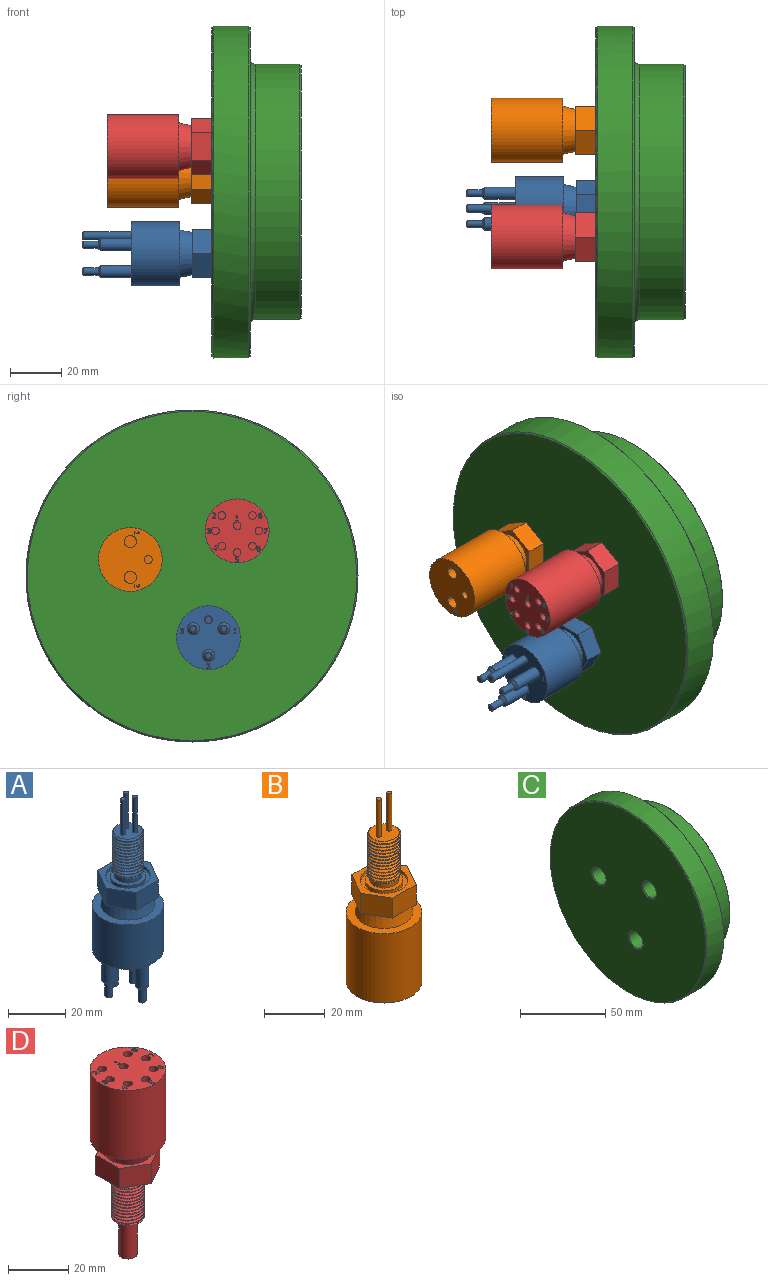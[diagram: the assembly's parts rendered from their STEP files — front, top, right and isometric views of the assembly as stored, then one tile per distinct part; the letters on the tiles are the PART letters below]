
ASSEMBLY  parts=4 mates=6
PART A: 107 faces, bbox 25.1x25.1x84.6 mm
  f0: bspline ~17.61x11.58mm, area 383.2mm2, adj f1,f2,f3,f4,f5,f6
  f1: cone r=5.31mm half-angle=45deg, axis (0,0,1), area 12.2mm2, adj f0,f2,f5,f6
  f2: cylinder r=5.56mm len=16mm, axis (0,0,1), area 187mm2, adj f0,f1,f3,f5
  f3: cone r=5.31mm half-angle=45deg, axis (0,0,-1), area 12.2mm2, adj f0,f2,f4,f5
  f4: plane 10.16x9.91mm, normal (0,0,1), area 72.4mm2, adj f0,f3,f5,f7,f8,f9
  f5: bspline ~17.61x11.58mm, area 382.1mm2, adj f0,f1,f2,f3,f4,f6
  f6: plane 10.17x10.16mm, normal (0,0,-1), area 79.2mm2, adj f0,f1,f5
  f7: cylinder r=0.85mm len=15mm, axis (0,0,1), area 80.1mm2, adj f4,f10
  f8: cylinder r=0.85mm len=15mm, axis (0,0,1), area 80.1mm2, adj f4,f11
  f9: cylinder r=0.85mm len=15mm, axis (0,0,1), area 80.1mm2, adj f4,f12
  f10: plane 1.7x1.7mm, normal (0,0,1), area 2.3mm2, adj f7
  f11: plane 1.7x1.7mm, normal (0,0,1), area 2.3mm2, adj f8
  f12: plane 1.7x1.7mm, normal (0,0,1), area 2.3mm2, adj f9
  f13: plane 9.56x9.56mm, normal (0,0,1), area 71.7mm2, adj f14
  f14: cylinder r=4.78mm len=9.56mm, axis (0,0,-1), area 60mm2, adj f13,f15
  f15: plane 12.5x12.5mm, normal (0,0,1), area 51mm2, adj f14,f16
  f16: cylinder r=6.25mm len=12.5mm, axis (0,0,-1), area 51.1mm2, adj f15,f17
  f17: plane 15.7x15.7mm, normal (0,0,1), area 70.9mm2, adj f16,f18
  f18: cylinder r=7.85mm len=15.7mm, axis (0,0,-1), area 64.1mm2, adj f17,f19
  f19: plane 21.94x19mm, normal (0,0,1), area 119mm2, adj f18,f20,f21,f22,f23,f24,f25
  f20: plane 10.97x7.5mm, normal (0,1,0), area 82.3mm2, adj f19,f21,f25,f26
  f21: plane 9.5x7.5mm, normal (-0.87,0.5,0), area 82.3mm2, adj f19,f20,f22,f26
  f22: plane 9.5x7.5mm, normal (-0.87,-0.5,0), area 82.3mm2, adj f19,f21,f23,f26
  f23: plane 10.97x7.5mm, normal (0,-1,0), area 82.3mm2, adj f19,f22,f24,f26
  f24: plane 9.5x7.5mm, normal (0.87,-0.5,0), area 82.3mm2, adj f19,f23,f25,f26
  f25: plane 9.5x7.5mm, normal (0.87,0.5,0), area 82.3mm2, adj f19,f20,f24,f26
  f26: plane 21.94x19mm, normal (0,0,-1), area 98.8mm2, adj f20,f21,f22,f23,f24,f25,f27
  f27: cone r=9.5mm half-angle=14deg, axis (0,0,-1), area 287.4mm2, adj f26,f28
  f28: plane 25x25mm, normal (0,0,1), area 207.3mm2, adj f27,f29
  f29: cylinder r=12.5mm len=25mm, axis (0,0,1), area 1492.3mm2, adj f28,f30
  f30: plane 25x25mm, normal (0,0,-1), area 425.9mm2, adj f29,f31,f32,f33,f34,f35,f36,f37
  f31: plane 0.23x0.1mm, normal (1,0,0), area 0mm2, adj f30,f32,f47,f90
  f32: plane 1.23x0.1mm, normal (0,1,0), area 0.1mm2, adj f30,f31,f33,f90
  f33: plane 0.28x0.1mm, normal (-1,0,0), area 0mm2, adj f30,f32,f34,f90
  f34: extruded ~0.48x0.48mm, area 0.1mm2, adj f30,f33,f35,f90
  f35: extruded ~0.71x0.4mm, area 0.1mm2, adj f30,f34,f36,f90
  f36: extruded ~0.25x0.1mm, area 0mm2, adj f30,f35,f37,f90
  f37: extruded ~0.24x0.1mm, area 0mm2, adj f30,f36,f38,f90
  f38: extruded ~0.28x0.1mm, area 0mm2, adj f30,f37,f39,f90
  f39: extruded ~0.19x0.11mm, area 0mm2, adj f30,f38,f40,f90
  f40: plane 0.1x0.01mm, normal (0,1,0), area 0mm2, adj f30,f39,f41,f90
  f41: plane 0.29x0.1mm, normal (-1,0,0), area 0mm2, adj f30,f40,f42,f90
  f42: extruded ~0.51x0.12mm, area 0.1mm2, adj f30,f41,f43,f90
  f43: extruded ~0.6x0.55mm, area 0.1mm2, adj f30,f42,f44,f90
  f44: extruded ~0.4x0.1mm, area 0mm2, adj f30,f43,f45,f90
  f45: extruded ~0.34x0.27mm, area 0mm2, adj f30,f44,f46,f90
  f46: extruded ~0.53x0.52mm, area 0.1mm2, adj f30,f45,f47,f90
  f47: plane 0.98x0.1mm, normal (0,-1,0), area 0.1mm2, adj f30,f31,f46,f90
  f48: plane 0.2x0.1mm, normal (1,0,0), area 0mm2, adj f30,f49,f58,f91
  f49: plane 0.98x0.1mm, normal (0,1,0), area 0.1mm2, adj f30,f48,f50,f91
  f50: plane 0.2x0.1mm, normal (-1,0,0), area 0mm2, adj f30,f49,f51,f91
  f51: plane 0.36x0.1mm, normal (0,-1,0), area 0mm2, adj f30,f50,f52,f91
  f52: plane 1.34x0.1mm, normal (-1,0,0), area 0.1mm2, adj f30,f51,f53,f91
  f53: plane 0.36x0.1mm, normal (0,1,0), area 0mm2, adj f30,f52,f54,f91
  f54: plane 0.18x0.1mm, normal (-1,0,0), area 0mm2, adj f30,f53,f55,f91
  f55: extruded ~0.41x0.28mm, area 0.1mm2, adj f30,f54,f56,f91
  f56: plane 0.21x0.1mm, normal (0,-1,0), area 0mm2, adj f30,f55,f57,f91
  f57: plane 1.8x0.1mm, normal (1,0,0), area 0.2mm2, adj f30,f56,f58,f91
  f58: plane 0.36x0.1mm, normal (0,-1,0), area 0mm2, adj f30,f48,f57,f91
  f59: extruded ~0.24x0.1mm, area 0mm2, adj f30,f60,f85,f92
  f60: extruded ~0.29x0.1mm, area 0mm2, adj f30,f59,f61,f92
  f61: extruded ~0.2x0.11mm, area 0mm2, adj f30,f60,f62,f92
  f62: plane 0.1x0.02mm, normal (0,1,0), area 0mm2, adj f30,f61,f63,f92
  f63: plane 0.28x0.1mm, normal (-1,0,0), area 0mm2, adj f30,f62,f64,f92
  f64: extruded ~0.52x0.12mm, area 0.1mm2, adj f30,f63,f65,f92
  f65: extruded ~0.42x0.11mm, area 0mm2, adj f30,f64,f66,f92
  f66: extruded ~0.37x0.18mm, area 0mm2, adj f30,f65,f67,f92
  f67: extruded ~0.45x0.37mm, area 0.1mm2, adj f30,f66,f68,f92
  f68: plane 0.1x0.02mm, normal (1,0,0), area 0mm2, adj f30,f67,f69,f92
  f69: extruded ~0.27x0.13mm, area 0mm2, adj f30,f68,f70,f92
  f70: extruded ~0.37x0.14mm, area 0mm2, adj f30,f69,f71,f92
  f71: cylinder r=0.63mm len=0.45mm, axis (0,0,1), area 0mm2, adj f30,f70,f72,f92
  f72: extruded ~0.49x0.18mm, area 0.1mm2, adj f30,f71,f73,f92
  f73: extruded ~0.55x0.12mm, area 0.1mm2, adj f30,f72,f74,f92
  f74: plane 0.28x0.1mm, normal (-1,0,0), area 0mm2, adj f30,f73,f75,f92
  f75: plane 0.1x0.02mm, normal (0,-1,0), area 0mm2, adj f30,f74,f76,f92
  f76: extruded ~0.51x0.18mm, area 0.1mm2, adj f30,f75,f77,f92
  f77: extruded ~0.3x0.11mm, area 0mm2, adj f30,f76,f78,f92
  f78: extruded ~0.31x0.11mm, area 0mm2, adj f30,f77,f79,f92
  f79: extruded ~0.29x0.12mm, area 0mm2, adj f30,f78,f80,f92
  f80: extruded ~0.3x0.1mm, area 0mm2, adj f30,f79,f81,f92
  f81: plane 0.11x0.1mm, normal (0,1,0), area 0mm2, adj f30,f80,f82,f92
  f82: plane 0.22x0.1mm, normal (-1,0,0), area 0mm2, adj f30,f81,f83,f92
  f83: plane 0.1x0.09mm, normal (0,-1,0), area 0mm2, adj f30,f82,f84,f92
  f84: extruded ~0.41x0.34mm, area 0.1mm2, adj f30,f83,f85,f92
  f85: extruded ~0.22x0.11mm, area 0mm2, adj f30,f59,f84,f92
  f86: cylinder r=2.4mm len=12mm, axis (0,0,-1), area 181mm2, adj f30,f93
  f87: cylinder r=2.4mm len=12mm, axis (0,0,-1), area 181mm2, adj f30,f94
  f88: cylinder r=2.4mm len=12mm, axis (0,0,-1), area 181mm2, adj f30,f95
  f89: cylinder r=1.6mm len=18.7mm, axis (0,0,-1), area 188mm2, adj f30,f96
  f90: plane 2.04x1.23mm, normal (0,0,-1), area 1mm2, adj f31,f32,f33,f34,f35,f36,f37,f38
  f91: plane 2.01x0.98mm, normal (0,0,-1), area 0.7mm2, adj f48,f49,f50,f51,f52,f53,f54,f55
  f92: plane 2.08x1.22mm, normal (0,0,-1), area 1mm2, adj f59,f60,f61,f62,f63,f64,f65,f66
  f93: cone r=1.9mm half-angle=45deg, axis (0,0,1), area 16.9mm2, adj f86,f97
  f94: cone r=1.9mm half-angle=45deg, axis (0,0,1), area 16.9mm2, adj f87,f98
  f95: cone r=1.9mm half-angle=45deg, axis (0,0,1), area 16.9mm2, adj f88,f99
  f96: cone r=1.45mm half-angle=45deg, axis (0,0,1), area 3.9mm2, adj f89,f100
  f97: cylinder r=1.4mm len=5.7mm, axis (0,0,-1), area 50.1mm2, adj f93,f101
  f98: cylinder r=1.4mm len=5.7mm, axis (0,0,-1), area 50.1mm2, adj f94,f102
  f99: cylinder r=1.4mm len=5.7mm, axis (0,0,-1), area 50.1mm2, adj f95,f103
  f100: plane 2.6x2.6mm, normal (0,0,-1), area 5.3mm2, adj f96
  f101: cone r=1.25mm half-angle=45deg, axis (0,0,1), area 3.3mm2, adj f97,f104
  f102: cone r=1.25mm half-angle=45deg, axis (0,0,1), area 3.3mm2, adj f98,f105
  f103: cone r=1.25mm half-angle=45deg, axis (0,0,1), area 3.3mm2, adj f99,f106
  f104: plane 2.2x2.2mm, normal (0,0,-1), area 3.8mm2, adj f101
  f105: plane 2.2x2.2mm, normal (0,0,-1), area 3.8mm2, adj f102
  f106: plane 2.2x2.2mm, normal (0,0,-1), area 3.8mm2, adj f103
PART B: 64 faces, bbox 25.1x25.1x75.1 mm
  f0: bspline ~17.61x11.58mm, area 383.3mm2, adj f1,f2,f3,f34,f35,f36,f39
  f1: bspline ~17.61x11.58mm, area 388.6mm2, adj f0,f2,f3,f34,f35,f36
  f2: plane 10.17x10.16mm, normal (0,0,-1), area 7.5mm2, adj f0,f1,f36,f39
  f3: cone r=5.31mm half-angle=45deg, axis (0,0,-1), area 12.2mm2, adj f0,f1,f34,f35
  f4: plane 0.23x0.1mm, normal (1,0,0), area 0mm2, adj f5,f20,f21,f61
  f5: plane 0.98x0.1mm, normal (0,-1,0), area 0.1mm2, adj f4,f6,f21,f61
  f6: extruded ~0.53x0.52mm, area 0.1mm2, adj f5,f7,f21,f61
  f7: extruded ~0.34x0.27mm, area 0mm2, adj f6,f8,f21,f61
  f8: extruded ~0.4x0.1mm, area 0mm2, adj f7,f9,f21,f61
  f9: extruded ~0.6x0.55mm, area 0.1mm2, adj f8,f10,f21,f61
  f10: extruded ~0.51x0.12mm, area 0.1mm2, adj f9,f11,f21,f61
  f11: plane 0.29x0.1mm, normal (-1,0,0), area 0mm2, adj f10,f12,f21,f61
  f12: plane 0.1x0.01mm, normal (0,1,0), area 0mm2, adj f11,f13,f21,f61
  f13: extruded ~0.19x0.11mm, area 0mm2, adj f12,f14,f21,f61
  f14: extruded ~0.28x0.1mm, area 0mm2, adj f13,f15,f21,f61
  f15: extruded ~0.24x0.1mm, area 0mm2, adj f14,f16,f21,f61
  f16: extruded ~0.25x0.1mm, area 0mm2, adj f15,f17,f21,f61
  f17: extruded ~0.71x0.4mm, area 0.1mm2, adj f16,f18,f21,f61
  f18: extruded ~0.48x0.48mm, area 0.1mm2, adj f17,f19,f21,f61
  f19: plane 0.28x0.1mm, normal (-1,0,0), area 0mm2, adj f18,f20,f21,f61
  f20: plane 1.23x0.1mm, normal (0,1,0), area 0.1mm2, adj f4,f19,f21,f61
  f21: plane 2.04x1.23mm, normal (0,0,-1), area 1mm2, adj f4,f5,f6,f7,f8,f9,f10,f11
  f22: plane 0.2x0.1mm, normal (1,0,0), area 0mm2, adj f23,f32,f33,f61
  f23: plane 0.36x0.1mm, normal (0,-1,0), area 0mm2, adj f22,f24,f33,f61
  f24: plane 1.8x0.1mm, normal (1,0,0), area 0.2mm2, adj f23,f25,f33,f61
  f25: plane 0.21x0.1mm, normal (0,-1,0), area 0mm2, adj f24,f26,f33,f61
  f26: extruded ~0.41x0.28mm, area 0.1mm2, adj f25,f27,f33,f61
  f27: plane 0.18x0.1mm, normal (-1,0,0), area 0mm2, adj f26,f28,f33,f61
  f28: plane 0.36x0.1mm, normal (0,1,0), area 0mm2, adj f27,f29,f33,f61
  f29: plane 1.34x0.1mm, normal (-1,0,0), area 0.1mm2, adj f28,f30,f33,f61
  f30: plane 0.36x0.1mm, normal (0,-1,0), area 0mm2, adj f29,f31,f33,f61
  f31: plane 0.2x0.1mm, normal (-1,0,0), area 0mm2, adj f30,f32,f33,f61
  f32: plane 0.98x0.1mm, normal (0,1,0), area 0.1mm2, adj f22,f31,f33,f61
  f33: plane 2.01x0.98mm, normal (0,0,-1), area 0.7mm2, adj f22,f23,f24,f25,f26,f27,f28,f29
  f34: cylinder r=5.56mm len=16mm, axis (0,0,1), area 131mm2, adj f0,f1,f3,f36
  f35: plane 10.16x9.9mm, normal (0,0,1), area 74.7mm2, adj f0,f1,f3,f37,f38
  f36: cone r=5.31mm half-angle=45deg, axis (0,0,1), area 12.2mm2, adj f0,f1,f2,f34
  f37: cylinder r=0.85mm len=15mm, axis (0,0,1), area 80.1mm2, adj f35,f63
  f38: cylinder r=0.85mm len=15mm, axis (0,0,1), area 80.1mm2, adj f35,f62
  f39: cylinder r=4.78mm len=9.56mm, axis (0,0,1), area 60mm2, adj f0,f2,f51
  f40: cylinder r=6.25mm len=12.5mm, axis (0,0,-1), area 51.1mm2, adj f42,f51
  f41: cylinder r=7.85mm len=15.7mm, axis (0,0,-1), area 64.1mm2, adj f42,f43
  f42: plane 15.7x15.7mm, normal (0,0,1), area 70.9mm2, adj f40,f41
  f43: plane 21.94x19mm, normal (0,0,1), area 119mm2, adj f41,f45,f46,f47,f48,f49,f50
  f44: plane 21.94x19mm, normal (0,0,-1), area 98.8mm2, adj f45,f46,f47,f48,f49,f50,f52
  f45: plane 10.97x8mm, normal (0,1,0), area 87.8mm2, adj f43,f44,f46,f50
  f46: plane 9.5x8mm, normal (0.87,0.5,0), area 87.8mm2, adj f43,f44,f45,f47
  f47: plane 9.5x8mm, normal (0.87,-0.5,0), area 87.8mm2, adj f43,f44,f46,f48
  f48: plane 10.97x8mm, normal (0,-1,0), area 87.8mm2, adj f43,f44,f47,f49
  f49: plane 9.5x8mm, normal (-0.87,-0.5,0), area 87.8mm2, adj f43,f44,f48,f50
  f50: plane 9.5x8mm, normal (-0.87,0.5,0), area 87.8mm2, adj f43,f44,f45,f49
  f51: plane 12.5x12.5mm, normal (0,0,1), area 51mm2, adj f39,f40
  f52: cone r=8.25mm half-angle=14deg, axis (0,0,-1), area 287.4mm2, adj f44,f60
  f53: cylinder r=2.4mm len=19mm, axis (0,0,1), area 286.5mm2, adj f54,f61
  f54: plane 4.8x4.8mm, normal (0,0,-1), area 18.1mm2, adj f53
  f55: cylinder r=2.4mm len=19mm, axis (0,0,1), area 286.5mm2, adj f56,f61
  f56: plane 4.8x4.8mm, normal (0,0,-1), area 18.1mm2, adj f55
  f57: cylinder r=1.6mm len=19mm, axis (0,0,1), area 191mm2, adj f58,f61
  f58: plane 3.2x3.2mm, normal (0,0,-1), area 8mm2, adj f57
  f59: cylinder r=12.5mm len=28mm, axis (0,0,1), area 2199.1mm2, adj f60,f61
  f60: plane 25x25mm, normal (0,0,1), area 207.3mm2, adj f52,f59
  f61: plane 25x25mm, normal (0,0,-1), area 444.9mm2, adj f4,f5,f6,f7,f8,f9,f10,f11
  f62: plane 1.7x1.7mm, normal (0,0,1), area 2.3mm2, adj f38
  f63: plane 1.7x1.7mm, normal (0,0,1), area 2.3mm2, adj f37
PART C: 18 faces, bbox 35x130x130 mm
  f0: cylinder r=5.56mm len=34mm, axis (1,0,0), area 1186.9mm2, adj f11,f13
  f1: cylinder r=5.56mm len=34mm, axis (1,0,0), area 1186.9mm2, adj f10,f12
  f2: plane 99x99mm, normal (1,0,0), area 7352mm2, adj f12,f13,f14,f15
  f3: cylinder r=50mm len=100mm, axis (-1,0,0), area 5497.8mm2, adj f8,f15
  f4: plane 129x129mm, normal (1,0,0), area 4574.9mm2, adj f8,f17
  f5: cylinder r=65mm len=130mm, axis (-1,0,0), area 5717.7mm2, adj f16,f17
  f6: plane 129x129mm, normal (-1,0,0), area 12724.2mm2, adj f9,f10,f11,f16
  f7: cylinder r=5.56mm len=34mm, axis (1,0,0), area 1186.9mm2, adj f9,f14
  f8: torus R=52mm, axis (-1,0,0), area 1001.3mm2, adj f3,f4
  f9: cone r=6.06mm half-angle=45deg, axis (-1,0,0), area 25.8mm2, adj f6,f7
  f10: cone r=6.06mm half-angle=45deg, axis (-1,0,0), area 25.8mm2, adj f1,f6
  f11: cone r=6.06mm half-angle=45deg, axis (-1,0,0), area 25.8mm2, adj f0,f6
  f12: cone r=5.56mm half-angle=45deg, axis (1,0,0), area 25.8mm2, adj f1,f2
  f13: cone r=5.56mm half-angle=45deg, axis (1,0,0), area 25.8mm2, adj f0,f2
  f14: cone r=5.56mm half-angle=45deg, axis (1,0,0), area 25.8mm2, adj f2,f7
  f15: cone r=50mm half-angle=45deg, axis (-1,0,0), area 221mm2, adj f2,f3
  f16: cone r=64.5mm half-angle=45deg, axis (1,0,0), area 287.7mm2, adj f5,f6
  f17: cone r=65mm half-angle=45deg, axis (-1,0,0), area 287.7mm2, adj f4,f5
PART D: 192 faces, bbox 25.1x25.1x75.1 mm
  f0: plane 2.08x1.3mm, normal (0,0,1), area 1.2mm2, adj f1,f2,f3,f4,f5,f6,f7,f8
  f1: extruded ~0.25x0.11mm, area 0mm2, adj f0,f2,f14,f188
  f2: extruded ~0.46x0.36mm, area 0.1mm2, adj f0,f1,f3,f188
  f3: extruded ~0.35x0.14mm, area 0mm2, adj f0,f2,f4,f188
  f4: extruded ~0.26x0.1mm, area 0mm2, adj f0,f3,f12,f188
  f5: plane 0.26x0.1mm, normal (-1,0,0), area 0mm2, adj f0,f6,f15,f149
  f6: plane 0.1x0.01mm, normal (0,1,0), area 0mm2, adj f0,f5,f7,f149
  f7: extruded ~0.25x0.1mm, area 0mm2, adj f0,f6,f8,f149
  f8: extruded ~0.67x0.59mm, area 0.1mm2, adj f0,f7,f9,f149
  f9: extruded ~0.42x0.14mm, area 0mm2, adj f0,f8,f10,f149
  f10: extruded ~0.39x0.12mm, area 0mm2, adj f0,f9,f11,f149
  f11: extruded ~0.51x0.22mm, area 0.1mm2, adj f0,f10,f21,f149
  f12: extruded ~0.36x0.11mm, area 0mm2, adj f0,f4,f13,f188
  f13: extruded ~0.13x0.1mm, area 0mm2, adj f0,f12,f14,f188
  f14: extruded ~0.53x0.14mm, area 0.1mm2, adj f0,f1,f13,f188
  f15: extruded ~0.23x0.1mm, area 0mm2, adj f0,f5,f16,f149
  f16: extruded ~0.68x0.32mm, area 0.1mm2, adj f0,f15,f17,f149
  f17: extruded ~0.84x0.22mm, area 0.1mm2, adj f0,f16,f18,f149
  f18: extruded ~0.74x0.22mm, area 0.1mm2, adj f0,f17,f19,f149
  f19: extruded ~0.44x0.18mm, area 0mm2, adj f0,f18,f20,f149
  f20: cylinder r=0.6mm len=0.45mm, axis (0,0,-1), area 0mm2, adj f0,f19,f21,f149
  f21: extruded ~0.5x0.19mm, area 0.1mm2, adj f0,f11,f20,f149
  f22: plane 0.24x0.1mm, normal (0,1,0), area 0mm2, adj f23,f28,f36,f149
  f23: plane 0.69x0.1mm, normal (-1,0,0), area 0.1mm2, adj f22,f24,f36,f149
  f24: plane 0.26x0.1mm, normal (0,1,0), area 0mm2, adj f23,f25,f36,f149
  f25: plane 0.69x0.1mm, normal (1,0,0), area 0.1mm2, adj f24,f26,f36,f149
  f26: plane 0.88x0.1mm, normal (0,1,0), area 0.1mm2, adj f25,f33,f36,f149
  f27: plane 0.67x0.1mm, normal (0,-1,0), area 0.1mm2, adj f34,f35,f36,f148
  f28: plane 0.22x0.1mm, normal (-1,0,0), area 0mm2, adj f22,f29,f36,f149
  f29: plane 0.24x0.1mm, normal (0,-1,0), area 0mm2, adj f28,f30,f36,f149
  f30: plane 1.1x0.1mm, normal (-1,0,0), area 0.1mm2, adj f29,f31,f36,f149
  f31: plane 0.25x0.1mm, normal (0,-1,0), area 0mm2, adj f30,f32,f36,f149
  f32: plane 1.03x0.89mm, normal (0.76,-0.66,0), area 0.1mm2, adj f31,f33,f36,f149
  f33: plane 0.28x0.1mm, normal (1,0,0), area 0mm2, adj f26,f32,f36,f149
  f34: plane 0.78x0.67mm, normal (-0.76,0.65,0), area 0.1mm2, adj f27,f35,f36,f148
  f35: plane 0.78x0.1mm, normal (1,0,0), area 0.1mm2, adj f27,f34,f36,f148
  f36: plane 2x1.38mm, normal (0,0,1), area 1mm2, adj f22,f23,f24,f25,f26,f27,f28,f29
  f37: plane 2.08x1.22mm, normal (0,0,1), area 1mm2, adj f38,f39,f40,f41,f42,f43,f44,f45
  f38: extruded ~0.55x0.12mm, area 0.1mm2, adj f37,f39,f52,f149
  f39: plane 0.28x0.1mm, normal (1,0,0), area 0mm2, adj f37,f38,f40,f149
  f40: plane 0.1x0.02mm, normal (0,-1,0), area 0mm2, adj f37,f39,f41,f149
  f41: extruded ~0.51x0.18mm, area 0.1mm2, adj f37,f40,f42,f149
  f42: extruded ~0.3x0.11mm, area 0mm2, adj f37,f41,f43,f149
  f43: extruded ~0.31x0.11mm, area 0mm2, adj f37,f42,f44,f149
  f44: extruded ~0.29x0.12mm, area 0mm2, adj f37,f43,f45,f149
  f45: extruded ~0.3x0.1mm, area 0mm2, adj f37,f44,f46,f149
  f46: plane 0.11x0.1mm, normal (0,1,0), area 0mm2, adj f37,f45,f47,f149
  f47: plane 0.22x0.1mm, normal (1,0,0), area 0mm2, adj f37,f46,f48,f149
  f48: plane 0.1x0.09mm, normal (0,-1,0), area 0mm2, adj f37,f47,f49,f149
  f49: extruded ~0.41x0.34mm, area 0.1mm2, adj f37,f48,f50,f149
  f50: extruded ~0.22x0.11mm, area 0mm2, adj f37,f49,f51,f149
  f51: extruded ~0.24x0.1mm, area 0mm2, adj f37,f50,f64,f149
  f52: extruded ~0.49x0.18mm, area 0.1mm2, adj f37,f38,f53,f149
  f53: cylinder r=0.63mm len=0.45mm, axis (0,0,-1), area 0mm2, adj f37,f52,f54,f149
  f54: extruded ~0.37x0.14mm, area 0mm2, adj f37,f53,f55,f149
  f55: extruded ~0.27x0.13mm, area 0mm2, adj f37,f54,f56,f149
  f56: plane 0.1x0.02mm, normal (-1,0,0), area 0mm2, adj f37,f55,f57,f149
  f57: extruded ~0.45x0.37mm, area 0.1mm2, adj f37,f56,f58,f149
  f58: extruded ~0.37x0.18mm, area 0mm2, adj f37,f57,f59,f149
  f59: extruded ~0.42x0.11mm, area 0mm2, adj f37,f58,f60,f149
  f60: extruded ~0.52x0.12mm, area 0.1mm2, adj f37,f59,f61,f149
  f61: plane 0.28x0.1mm, normal (1,0,0), area 0mm2, adj f37,f60,f62,f149
  f62: plane 0.1x0.02mm, normal (0,1,0), area 0mm2, adj f37,f61,f63,f149
  f63: extruded ~0.2x0.11mm, area 0mm2, adj f37,f62,f64,f149
  f64: extruded ~0.29x0.1mm, area 0mm2, adj f37,f51,f63,f149
  f65: plane 1.7x0.87mm, normal (-0.89,0.45,0), area 0.2mm2, adj f66,f68,f72,f149
  f66: plane 0.29x0.1mm, normal (0,1,0), area 0mm2, adj f65,f67,f72,f149
  f67: plane 1.77x0.91mm, normal (0.89,-0.46,0), area 0.2mm2, adj f66,f71,f72,f149
  f68: plane 0.3x0.1mm, normal (-1,0,0), area 0mm2, adj f65,f69,f72,f149
  f69: plane 1.27x0.1mm, normal (0,-1,0), area 0.1mm2, adj f68,f70,f72,f149
  f70: plane 0.24x0.1mm, normal (1,0,0), area 0mm2, adj f69,f71,f72,f149
  f71: plane 1.03x0.1mm, normal (0,1,0), area 0.1mm2, adj f67,f70,f72,f149
  f72: plane 2x1.27mm, normal (0,0,1), area 0.8mm2, adj f65,f66,f67,f68,f69,f70,f71
  f73: plane 2.04x1.23mm, normal (0,0,1), area 1mm2, adj f74,f75,f76,f77,f78,f79,f80,f81
  f74: plane 0.1x0.01mm, normal (0,1,0), area 0mm2, adj f73,f75,f83,f149
  f75: plane 0.29x0.1mm, normal (1,0,0), area 0mm2, adj f73,f74,f76,f149
  f76: extruded ~0.51x0.12mm, area 0.1mm2, adj f73,f75,f77,f149
  f77: extruded ~0.6x0.55mm, area 0.1mm2, adj f73,f76,f78,f149
  f78: extruded ~0.4x0.1mm, area 0mm2, adj f73,f77,f79,f149
  f79: extruded ~0.34x0.27mm, area 0mm2, adj f73,f78,f80,f149
  f80: extruded ~0.53x0.52mm, area 0.1mm2, adj f73,f79,f81,f149
  f81: plane 0.98x0.1mm, normal (0,-1,0), area 0.1mm2, adj f73,f80,f82,f149
  f82: plane 0.23x0.1mm, normal (-1,0,0), area 0mm2, adj f73,f81,f90,f149
  f83: extruded ~0.19x0.11mm, area 0mm2, adj f73,f74,f84,f149
  f84: extruded ~0.28x0.1mm, area 0mm2, adj f73,f83,f85,f149
  f85: extruded ~0.24x0.1mm, area 0mm2, adj f73,f84,f86,f149
  f86: extruded ~0.25x0.1mm, area 0mm2, adj f73,f85,f87,f149
  f87: extruded ~0.71x0.4mm, area 0.1mm2, adj f73,f86,f88,f149
  f88: extruded ~0.48x0.48mm, area 0.1mm2, adj f73,f87,f89,f149
  f89: plane 0.28x0.1mm, normal (1,0,0), area 0mm2, adj f73,f88,f90,f149
  f90: plane 1.23x0.1mm, normal (0,1,0), area 0.1mm2, adj f73,f82,f89,f149
  f91: extruded ~0.48x0.17mm, area 0.1mm2, adj f92,f100,f112,f149
  f92: extruded ~0.43x0.17mm, area 0mm2, adj f91,f93,f112,f149
  f93: extruded ~0.52x0.34mm, area 0.1mm2, adj f92,f94,f112,f149
  f94: plane 0.1x0.01mm, normal (1,0,0), area 0mm2, adj f93,f95,f112,f149
  f95: extruded ~0.44x0.29mm, area 0.1mm2, adj f94,f105,f112,f149
  f96: extruded ~0.42x0.38mm, area 0.1mm2, adj f97,f108,f112,f147
  f97: extruded ~0.43x0.23mm, area 0.1mm2, adj f96,f106,f112,f147
  f98: extruded ~0.28x0.12mm, area 0mm2, adj f99,f111,f112,f146
  f99: extruded ~0.29x0.19mm, area 0mm2, adj f98,f109,f112,f146
  f100: extruded ~0.65x0.6mm, area 0.1mm2, adj f91,f101,f112,f149
  f101: extruded ~0.5x0.36mm, area 0.1mm2, adj f100,f102,f112,f149
  f102: plane 0.1x0.01mm, normal (-1,0,0), area 0mm2, adj f101,f103,f112,f149
  f103: extruded ~0.47x0.3mm, area 0.1mm2, adj f102,f104,f112,f149
  f104: extruded ~0.6x0.51mm, area 0.1mm2, adj f103,f105,f112,f149
  f105: extruded ~0.6x0.53mm, area 0.1mm2, adj f95,f104,f112,f149
  f106: extruded ~0.29x0.12mm, area 0mm2, adj f97,f107,f112,f147
  f107: extruded ~0.34x0.24mm, area 0mm2, adj f106,f108,f112,f147
  f108: extruded ~0.38x0.37mm, area 0.1mm2, adj f96,f107,f112,f147
  f109: extruded ~0.33x0.3mm, area 0.1mm2, adj f99,f110,f112,f146
  f110: extruded ~0.34x0.31mm, area 0.1mm2, adj f109,f111,f112,f146
  f111: extruded ~0.4x0.2mm, area 0mm2, adj f98,f110,f112,f146
  f112: plane 2.09x1.3mm, normal (0,0,1), area 1.3mm2, adj f91,f92,f93,f94,f95,f96,f97,f98
  f113: plane 2.04x1.19mm, normal (0,0,1), area 1.1mm2, adj f114,f115,f116,f117,f118,f119,f120,f121
  f114: extruded ~0.33x0.1mm, area 0mm2, adj f113,f115,f124,f149
  f115: extruded ~0.4x0.1mm, area 0mm2, adj f113,f114,f116,f149
  f116: plane 1.03x0.1mm, normal (1,0,0), area 0.1mm2, adj f113,f115,f117,f149
  f117: plane 1.1x0.1mm, normal (0,-1,0), area 0.1mm2, adj f113,f116,f118,f149
  f118: plane 0.24x0.1mm, normal (-1,0,0), area 0mm2, adj f113,f117,f119,f149
  f119: plane 0.84x0.1mm, normal (0,1,0), area 0.1mm2, adj f113,f118,f120,f149
  f120: plane 0.53x0.1mm, normal (-1,0,0), area 0.1mm2, adj f113,f119,f121,f149
  f121: extruded ~0.18x0.1mm, area 0mm2, adj f113,f120,f122,f149
  f122: extruded ~0.46x0.12mm, area 0mm2, adj f113,f121,f123,f149
  f123: extruded ~0.48x0.21mm, area 0.1mm2, adj f113,f122,f133,f149
  f124: extruded ~0.29x0.11mm, area 0mm2, adj f113,f114,f125,f149
  f125: extruded ~0.33x0.1mm, area 0mm2, adj f113,f124,f126,f149
  f126: extruded ~0.29x0.12mm, area 0mm2, adj f113,f125,f127,f149
  f127: extruded ~0.29x0.1mm, area 0mm2, adj f113,f126,f128,f149
  f128: extruded ~0.22x0.11mm, area 0mm2, adj f113,f127,f129,f149
  f129: plane 0.1x0.02mm, normal (0,-1,0), area 0mm2, adj f113,f128,f130,f149
  f130: plane 0.28x0.1mm, normal (1,0,0), area 0mm2, adj f113,f129,f131,f149
  f131: cylinder r=1.27mm len=0.52mm, axis (0,0,-1), area 0.1mm2, adj f113,f130,f132,f149
  f132: extruded ~0.49x0.2mm, area 0.1mm2, adj f113,f131,f133,f149
  f133: extruded ~0.48x0.18mm, area 0.1mm2, adj f113,f123,f132,f149
  f134: plane 0.98x0.1mm, normal (0,1,0), area 0.1mm2, adj f135,f139,f145,f149
  f135: plane 0.2x0.1mm, normal (1,0,0), area 0mm2, adj f134,f136,f145,f149
  f136: plane 0.36x0.1mm, normal (0,-1,0), area 0mm2, adj f135,f137,f145,f149
  f137: plane 1.34x0.1mm, normal (1,0,0), area 0.1mm2, adj f136,f138,f145,f149
  f138: plane 0.36x0.1mm, normal (0,1,0), area 0mm2, adj f137,f144,f145,f149
  f139: plane 0.2x0.1mm, normal (-1,0,0), area 0mm2, adj f134,f140,f145,f149
  f140: plane 0.36x0.1mm, normal (0,-1,0), area 0mm2, adj f139,f141,f145,f149
  f141: plane 1.8x0.1mm, normal (-1,0,0), area 0.2mm2, adj f140,f142,f145,f149
  f142: plane 0.21x0.1mm, normal (0,-1,0), area 0mm2, adj f141,f143,f145,f149
  f143: extruded ~0.41x0.28mm, area 0.1mm2, adj f142,f144,f145,f149
  f144: plane 0.18x0.1mm, normal (1,0,0), area 0mm2, adj f138,f143,f145,f149
  f145: plane 2.01x0.98mm, normal (0,0,1), area 0.7mm2, adj f134,f135,f136,f137,f138,f139,f140,f141
  f146: plane 0.71x0.67mm, normal (0,0,1), area 0.4mm2, adj f98,f99,f109,f110,f111
  f147: plane 0.85x0.76mm, normal (0,0,1), area 0.5mm2, adj f96,f97,f106,f107,f108
  f148: plane 0.78x0.67mm, normal (0,0,1), area 0.3mm2, adj f27,f34,f35
  f149: plane 25x25mm, normal (0,0,1), area 424.7mm2, adj f5,f6,f7,f8,f9,f10,f11,f15
  f150: bspline ~17.61x11.58mm, area 384.7mm2, adj f151,f152,f153,f154,f155,f174
  f151: bspline ~17.61x11.58mm, area 383.3mm2, adj f150,f152,f153,f154,f155,f174
  f152: cone r=5.31mm half-angle=45deg, axis (0,0,1), area 12.2mm2, adj f150,f151,f154,f174
  f153: plane 10.17x10.16mm, normal (0,0,1), area 14mm2, adj f150,f151,f155,f156
  f154: cylinder r=5.56mm len=16mm, axis (0,0,-1), area 145.1mm2, adj f150,f151,f152,f155
  f155: cone r=5.31mm half-angle=45deg, axis (0,0,-1), area 12.2mm2, adj f150,f151,f153,f154
  f156: cylinder r=4.56mm len=9.11mm, axis (0,0,-1), area 57.3mm2, adj f153,f186
  f157: cylinder r=1.5mm len=15mm, axis (0,0,-1), area 141.4mm2, adj f149,f158
  f158: plane 3x3mm, normal (0,0,1), area 7.1mm2, adj f157
  f159: cylinder r=1.5mm len=15mm, axis (0,0,-1), area 141.4mm2, adj f149,f160
  f160: plane 3x3mm, normal (0,0,1), area 7.1mm2, adj f159
  f161: cylinder r=1.5mm len=15mm, axis (0,0,-1), area 141.4mm2, adj f149,f162
  f162: plane 3x3mm, normal (0,0,1), area 7.1mm2, adj f161
  f163: cylinder r=1.5mm len=15mm, axis (0,0,-1), area 141.4mm2, adj f149,f164
  f164: plane 3x3mm, normal (0,0,1), area 7.1mm2, adj f163
  f165: cylinder r=1.5mm len=15mm, axis (0,0,-1), area 141.4mm2, adj f149,f166
  f166: plane 3x3mm, normal (0,0,1), area 7.1mm2, adj f165
  f167: cylinder r=1.5mm len=15mm, axis (0,0,-1), area 141.4mm2, adj f149,f168
  f168: plane 3x3mm, normal (0,0,1), area 7.1mm2, adj f167
  f169: cylinder r=1.5mm len=15mm, axis (0,0,-1), area 141.4mm2, adj f149,f170
  f170: plane 3x3mm, normal (0,0,1), area 7.1mm2, adj f169
  f171: cylinder r=1.5mm len=15mm, axis (0,0,-1), area 141.4mm2, adj f149,f172
  f172: plane 3x3mm, normal (0,0,1), area 7.1mm2, adj f171
  f173: cylinder r=3mm len=15mm, axis (0,0,-1), area 282.7mm2, adj f174,f191
  f174: plane 10.17x9.91mm, normal (0,0,-1), area 50.9mm2, adj f150,f151,f152,f173
  f175: cylinder r=6.33mm len=12.65mm, axis (0,0,1), area 51.7mm2, adj f177,f186
  f176: cylinder r=8.57mm len=17.15mm, axis (0,0,1), area 70mm2, adj f177,f178
  f177: plane 17.15x17.15mm, normal (0,0,-1), area 105.3mm2, adj f175,f176
  f178: plane 21.94x19mm, normal (0,0,-1), area 81.6mm2, adj f176,f180,f181,f182,f183,f184,f185
  f179: plane 21.94x19mm, normal (0,0,1), area 98.8mm2, adj f180,f181,f182,f183,f184,f185,f187
  f180: plane 9.5x8mm, normal (0.5,0.87,0), area 87.8mm2, adj f178,f179,f181,f185
  f181: plane 9.5x8mm, normal (-0.5,0.87,0), area 87.8mm2, adj f178,f179,f180,f182
  f182: plane 10.97x8mm, normal (-1,0,0), area 87.8mm2, adj f178,f179,f181,f183
  f183: plane 9.5x8mm, normal (-0.5,-0.87,0), area 87.8mm2, adj f178,f179,f182,f184
  f184: plane 9.5x8mm, normal (0.5,-0.87,0), area 87.8mm2, adj f178,f179,f183,f185
  f185: plane 10.97x8mm, normal (1,0,0), area 87.8mm2, adj f178,f179,f180,f184
  f186: plane 12.65x12.65mm, normal (0,0,-1), area 60.5mm2, adj f156,f175
  f187: cone r=8.25mm half-angle=14deg, axis (0,0,1), area 287.4mm2, adj f179,f190
  f188: plane 0.88x0.75mm, normal (0,0,1), area 0.5mm2, adj f1,f2,f3,f4,f12,f13,f14
  f189: cylinder r=12.5mm len=28mm, axis (0,0,-1), area 2199.1mm2, adj f149,f190
  f190: plane 25x25mm, normal (0,0,-1), area 207.3mm2, adj f187,f189
  f191: plane 6x6mm, normal (0,0,-1), area 28.3mm2, adj f173
PLACE A rot(axis=(0.58,0.58,0.58),120deg) t=(-66,46.06,-6.17)mm
PLACE B rot(axis=(0.71,0,0.71),180deg) t=(-75.5,76.68,24.45)mm
PLACE C t=(0.5,52.53,17.98)mm fixed
PLACE D rot(axis=(0.58,-0.58,-0.58),120deg) t=(-52.5,34.85,35.66)mm
MATE cylindrical B.f39 <-> C.f1  axis (1,0,0) through (-61.5,76.68,24.45)mm
MATE planar C.f3 <-> A.f19  axis (-1,0,0) through (-34.5,52.53,17.98)mm
MATE planar C.f3 <-> B.f39  axis (-1,0,0) through (-34.5,52.53,17.98)mm
MATE slider A.f14 <-> C.f0  axis (1,0,0) through (-47,46.06,-6.17)mm
MATE slider D.f156 <-> C.f7  axis (1,0,0) through (-47.5,34.85,35.66)mm
MATE planar C.f7 <-> D.f178  axis (-1,0,0) through (-34.5,34.85,35.66)mm
